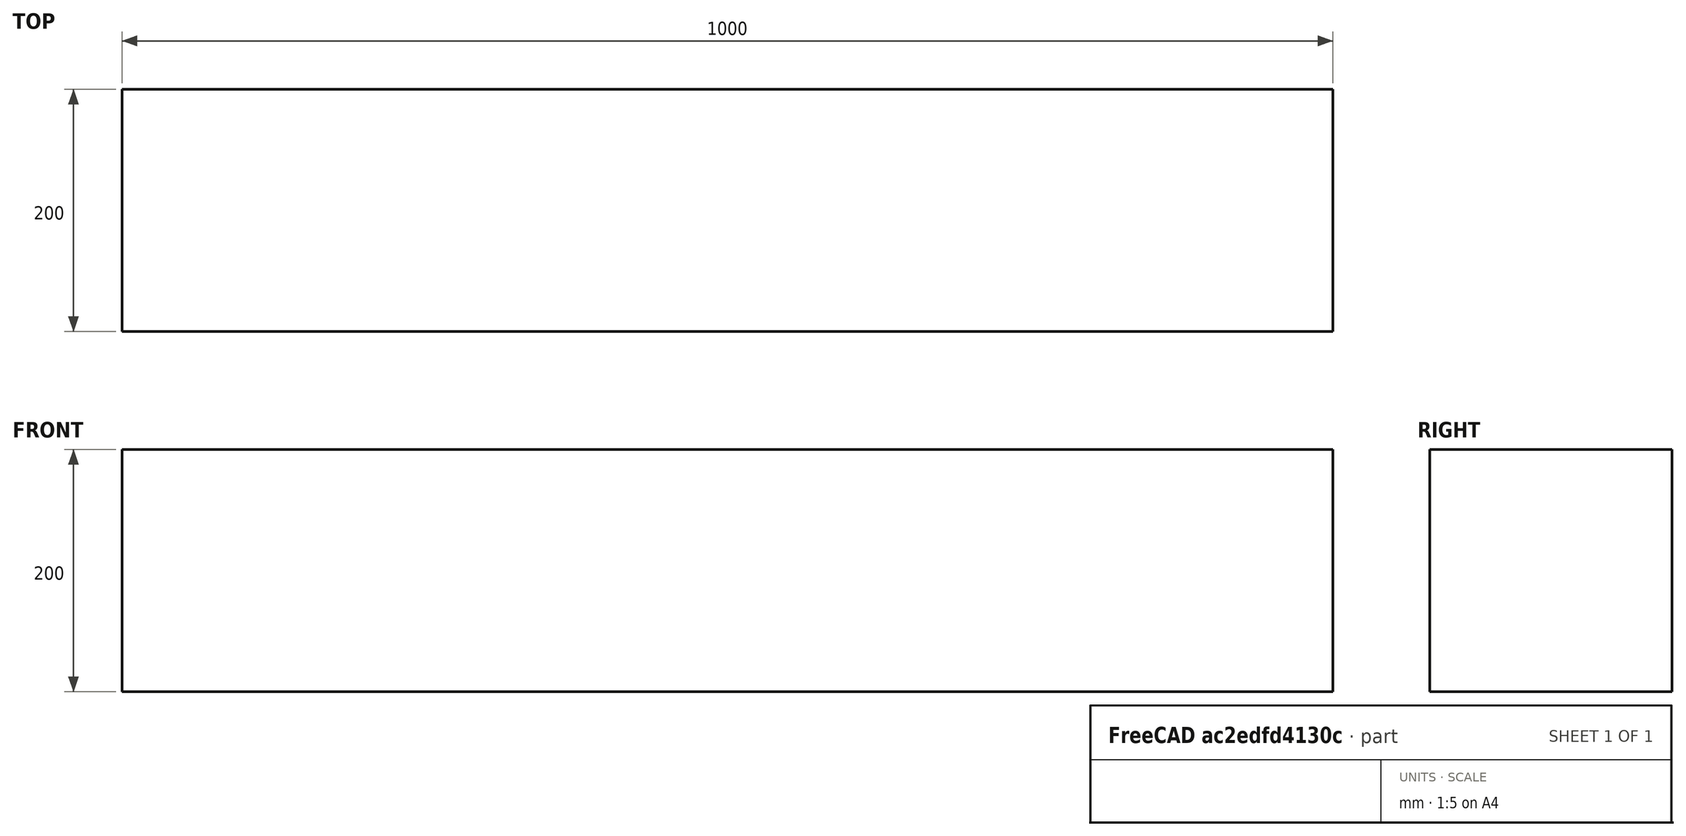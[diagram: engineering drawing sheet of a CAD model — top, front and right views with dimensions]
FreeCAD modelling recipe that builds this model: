
FCSTD DOCUMENT  (FreeCAD 0.16R6706 (Git))
Label: part_tolerance
License: All rights reserved
LicenseURL: http://en.wikipedia.org/wiki/All_rights_reserved
objects: Part::Box×1, Drawing::FeatureViewPart×1, Drawing::FeatureViewPython×1, Drawing::FeaturePage×1
note: 1 computed .brp shape members not serialized (recipe doc carries the construction recipe); baked Part::Feature solids carry a one-line shape summary decoded from their .brp

FEATURE [Part::Box] Box  label="Cube"
  Height = 200
  Length = 1000
  Width = 200
FEATURE [Drawing::FeatureViewPart] View
  Direction = (1,-1,1)
  HiddenWidth = 0.15
  LineWidth = 0.35
  Rotation = 60
  Scale = 0.1
  ShowHiddenLines = true
  ShowSmoothLines = false
  Source = -> Box
  Tolerance = 0.05
  ViewResult = <g id="View"\n   transform="rotate(60,80.2513,162.789) translate(80.2513,162.789) scale(0.1,0.1)"\n  >\n<g   stroke="rgb(0, 0, 0)"\n   stroke-width="1.5"\n   stroke-linecap="butt"\n   stroke-linejoin="miter"\n   stroke-dasharray="0.2,0.1"\n   fill="none"\n   transform="scale(1,-1)"\n  >\n<path id= "1" d=" M 0 163.299 L -141.421 244.949 " />\n<path id= "2" d=" M 0 0 L 0 163.299 " />\n<path id= "3" d=" M 0 163.299 L 707.107 571.548 " />\n</g>\n<g   stroke="rgb(0, 0, 0)"\n   stroke-width="3.5"\n   stroke-linecap="butt"\n   stroke-linejoin="miter"\n   fill="none"\n   transform="scale(1,-1)"\n  >\n<path id= "1" d=" M 0 0 L -141.421 81.6497 " />\n<path id= "2" d=" M -141.421 81.6497 L -141.421 244.949 " />\n<path id= "3" d=" M 707.107 408.248 L 565.685 489.898 " />\n<path id= "4" d=" M 565.685 489.898 L 565.685 653.197 " />\n<path id= "5" d=" M 707.107 571.548 L 565.685 653.197 " />\n<path id= "6" d=" M 707.107 408.248 L 707.107 571.548 " />\n<path id= "7" d=" M 0 0 L 707.107 408.248 " />\n<path id= "8" d=" M -141.421 81.6497 L 565.685 489.898 " />\n<path id= "9" d=" M -141.421 244.949 L 565.685 653.197 " />\n</g>\n</g>
  Visible = true
  X = 80.2513
  Y = 162.789
FEATURE [Drawing::FeatureViewPython] dim001  # drawing view (typed FeaturePython)
  Rotation = 0
  ViewResult = <g> \n  <line x1="79.251299" y1="164.521050" x2="61.255370" y2="195.690883" style="stroke:rgb(153,153,153);stroke-width:0.30" />\n<line x1="149.961963" y1="205.345913" x2="131.966034" y2="236.515745" style="stroke:rgb(153,153,153);stroke-width:0.30" />\n<line x1="61.755370" y1="194.824858" x2="132.466034" y2="235.649720" style="stroke:rgb(153,153,153);stroke-width:0.30" /> \n  <polygon points="132.466034,235.649720 130.367959,233.283694 129.001933,233.649719 129.367958,235.015744" style="fill:rgb(153,153,153);stroke:rgb(153,153,153);stroke-width:0" /><polygon points="61.755370,194.824858 63.853445,197.190884 65.219471,196.824859 64.853446,195.458834" style="fill:rgb(153,153,153);stroke:rgb(153,153,153);stroke-width:0" /> \n  <text x="95.378652" y="214.237288" font-family="Verdana" font-size="3.6" fill="rgb(153,153,153)" text-anchor="middle" transform="rotate(-59.999975 95.378652,214.237288)" >816.497</text> </g>
  Visible = true
  X = 0
  Y = 0
  arrowL1 = 3
  arrowL2 = 1
  arrowW = 2
  arrow_scheme = 0
  autoPlaceOffset = 2
  autoPlaceText = true
  click1_x = 79.126
  click1_y = 204.854
  click2_x = 79.126
  click2_y = 204.854
  comma_decimal_place = false
  dimension_line_overshoot = 1
  gap_datum_points = 2
  halfDimension_linear = false
  lineColor = rgb(153,153,153)
  strokeWidth = 0.3
  textFormat_linear = %(value)3.3f
  textRenderer_color = rgb(153,153,153)
  textRenderer_family = Verdana
  textRenderer_size = 3.6
  unit_custom_scale = 1
  unit_scheme = 0
FEATURE [Drawing::FeaturePage] Page
  Group = -> [View,dim001]
